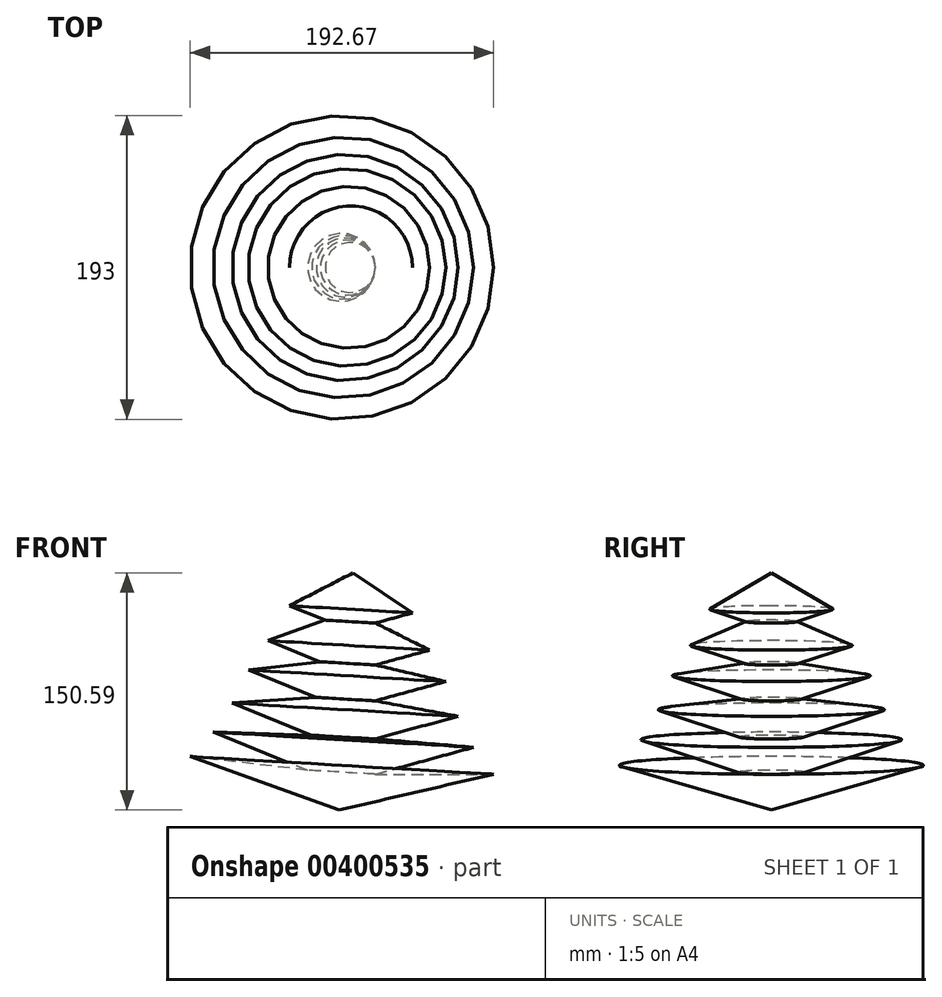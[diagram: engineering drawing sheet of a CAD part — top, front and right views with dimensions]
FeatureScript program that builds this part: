
annotation { "Feature Type Name" : "Feature", "Feature Type Description" : "" }
export const myFeature = defineFeature(function(context is Context, id is Id, definition is map)
    precondition{}
    {
        {
            var Q0;
            Q0=qCreatedBy(makeId("Front.planeOp"),FACE);
            var sketch = newSketch(context, id + "F0", { "sketchPlane" : qUnion([Q0])});
            skLineSegment(sketch, "E0", {"start": v(-14.1, 75.24) * mm, "end": v(-22.91, -75.35) * mm});
            skLineSegment(sketch, "E1", {"start": v(-14.1, 75.24) * mm, "end": v(23.62, 49.82) * mm});
            skLineSegment(sketch, "E2", {"start": v(23.62, 49.82) * mm, "end": v(0, 43.36) * mm});
            skLineSegment(sketch, "E3", {"start": v(0, 43.36) * mm, "end": v(34.54, 26.19) * mm});
            skLineSegment(sketch, "E4", {"start": v(34.54, 26.19) * mm, "end": v(0, 16.73) * mm});
            skLineSegment(sketch, "E5", {"start": v(0, 16.73) * mm, "end": v(44.77, 6.23) * mm});
            skLineSegment(sketch, "E6", {"start": v(44.77, 6.23) * mm, "end": v(0, -6.03) * mm});
            skLineSegment(sketch, "E7", {"start": v(0, -6.03) * mm, "end": v(52.52, -15.86) * mm});
            skLineSegment(sketch, "E8", {"start": v(52.52, -15.86) * mm, "end": v(0, -30.24) * mm});
            skLineSegment(sketch, "E9", {"start": v(0, -30.24) * mm, "end": v(62.4, -35.57) * mm});
            skLineSegment(sketch, "E10", {"start": v(62.4, -35.57) * mm, "end": v(0, -52.65) * mm});
            skLineSegment(sketch, "E11", {"start": v(0, -52.65) * mm, "end": v(75.08, -52.65) * mm});
            skLineSegment(sketch, "E12", {"start": v(75.08, -52.65) * mm, "end": v(-22.91, -75.35) * mm});
            skSolve(sketch);
        }
        {
            var Q0;
            Q0=makeQuery(id+"F0.imprint","IMPRINT",FACE,{"disambiguationData":[TD([[makeQuery(id+"F0.imprint","IMPRINT",EDGE,{"derivedFrom":sQuery(id+"F0.wireOp",EDGE,"E0")}),1.0]])]});
            var Q1;
            Q1=sQuery(id+"F0.wireOp",EDGE,"E0");
            revolve(context, id + "F1", {"entities" : qUnion([Q0]), "axis" : qUnion([Q1]), "revolveType" : RevolveType.FULL});
        }
    });
